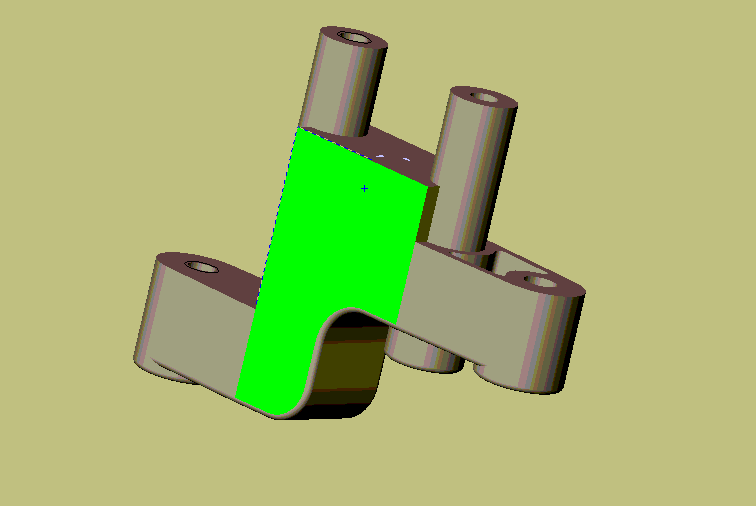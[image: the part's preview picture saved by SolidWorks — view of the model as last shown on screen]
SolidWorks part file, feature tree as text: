
SOLIDWORKS PART (.sldprt)
format: sldprt  version: not decoded by parser v0  size: 412,160 bytes
history: native  units: mm
features: sketch x19, extrude x8, fillet x4, hole x4, thread x4, plane x3, cut_extrude x3, material x1 (+8 scaffold rows collapsed)
feature tree (54):
  scaffold x8  (default folders/planes/origin — collapsed)
  material  "Matériau <non spécifié>"
  plane  "Plane1"
  plane  "Plane2"
  plane  "Plane3"
  sketch  "Esquisse1"  dims[c1.D1=6.0mm c1.D3=3.0mm c2.D1=3.0mm c2.D2=17.0mm c2.D3=9.0mm c2.D4=4.5mm c3.D2=1.5mm c3.D3=1.5mm c3.D4=8.0mm c4.D3=8.0mm]
  extrude  "Base-Extrusion"  Depth=5mm
  sketch  "Esquisse2"  dims[D1=3.0mm D2=3.0mm]
  extrude  "Boss.-Extru.1"  Depth=8mm
  sketch  "Esquisse3"  dims[c1.D2=8.0mm c1.D1=14.0mm c1.D3=0.5mm c2.D1=10.0mm c2.D3=0.5mm c2.D4=~10.012492mm c3.D1=11.0mm]
  extrude  "Boss.-Extru.4"  Depth=8mm
  sketch  "Esquisse4"
  extrude  "Boss.-Extru.5"  Depth=1mm
  sketch  "Esquisse6"  dims[D2=8.0mm D1=19.0mm D3=~6.222939mm]
  extrude  "Boss.-Extru.6"  Depth=12mm
  sketch  "Esquisse7"  dims[D1=9.0mm]
  cut_extrude  "Enlèv. mat.-Extru.2"  Depth=3.5mm
  sketch  "Esquisse8"
  extrude  "Boss.-Extru.7"  [1 undecoded]
  sketch  "Esquisse9"  dims[D1=8.0mm]
  extrude  "Boss.-Extru.8"  Depth=1mm
  fillet  "Congé4"  Radius=0.5mm
  hole  "Perçage4"  Diameter=2.5mm Depth=9.5mm
  sketch  "Esquisse18"
  sketch  "Esquisse17"  dims[hole-wizard template sketch: 60 standard entries collapsed; hole parameters kept: c18.Profondeur du perçage jusqu'au prochain=9.5mm]
  thread  "Représentation de filetage4"  Diameter=6mm  [1 undecoded]
  sketch  "Esquisse19"  dims[D1=7.0mm D2=11.0mm]
  extrude  "Boss.-Extru.9"  Depth=3mm
  fillet  "Congé6"  Radius=0.5mm
  hole  "Perçage5"  Diameter=2.05mm Depth=7.25mm
  sketch  "Esquisse21"
  sketch  "Esquisse20"  dims[hole-wizard template sketch: 46 standard entries collapsed; hole parameters kept: c15.Diamètre du perçage=2.05mm c15.Profondeur du perçage=7.25mm c15.D3=~14.816244mm c15.Angle de pointe=180.0deg]
  thread  "Représentation de filetage5"  Diameter=5mm  [1 undecoded]
  sketch  "Esquisse22"  dims[D1=0.5mm]
  cut_extrude  "Enlèv. mat.-Extru.3"  Depth=2.5mm
  fillet  "Congé8"  Radius=4mm
  fillet  "Congé9"  Radius=0.5mm
  hole  "Perçage6"  Diameter=2.5mm Depth=8.5mm
  sketch  "Esquisse24"
  sketch  "Esquisse23"  dims[hole-wizard template sketch: 47 standard entries collapsed; hole parameters kept: c15.Profondeur du perçage=8.5mm c15.D3=~14.816244mm c15.Angle de pointe=180.0deg]
  thread  "Représentation de filetage6"  Diameter=6mm  [1 undecoded]
  hole  "Perçage7"  Diameter=2.5mm Depth=8.5mm
  sketch  "Esquisse26"
  sketch  "Esquisse25"  dims[hole-wizard template sketch: 47 standard entries collapsed; hole parameters kept: c15.Profondeur du perçage=8.5mm c15.D3=~14.816244mm c15.Angle de pointe=180.0deg]
  thread  "Représentation de filetage7"  Diameter=6mm  [1 undecoded]
  sketch  "Esquisse27"  dims[D1=3.0mm]
  cut_extrude  "Enlèv. mat.-Extru.4"  [1 undecoded]
decode coverage: 34 of 42 modeling features carry decoded parameters
note: ~ marks probable driven/reference dimensions
note: 6 parameter values undecoded
summary: Diameter pulled from absorbed wizard sketch
note: suppression state not decoded; provenance and decode notes live in map.json
